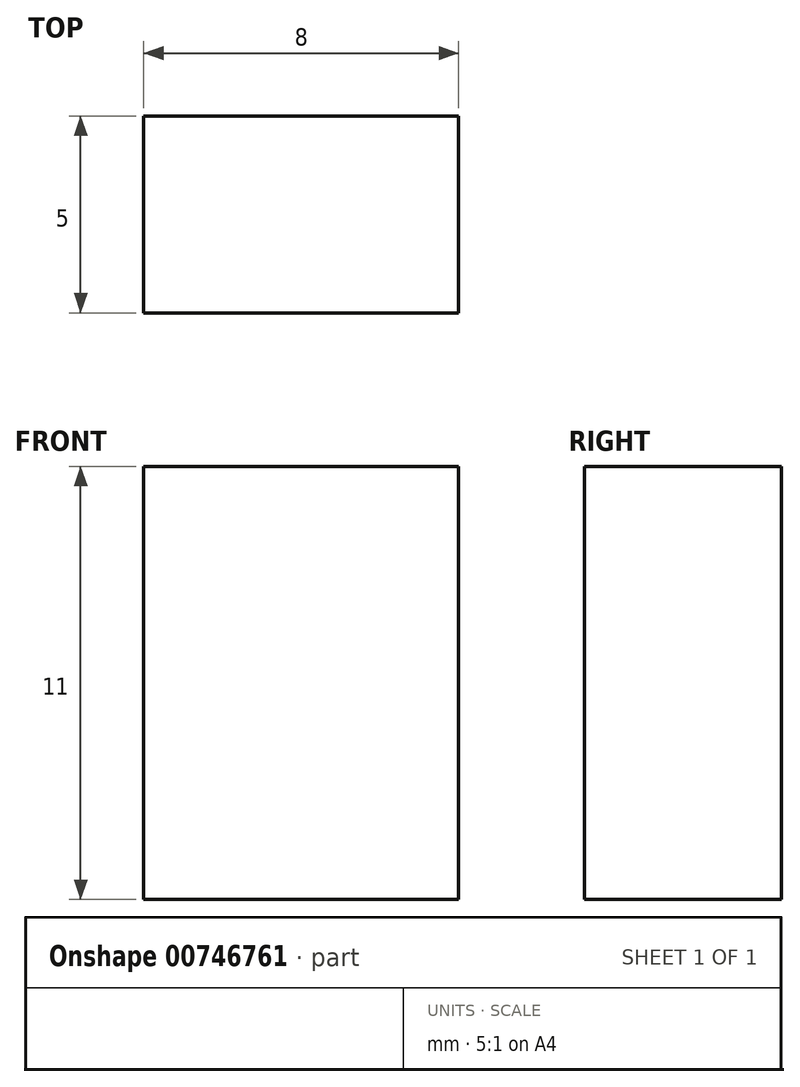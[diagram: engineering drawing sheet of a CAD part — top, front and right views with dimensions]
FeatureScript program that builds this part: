
annotation { "Feature Type Name" : "Feature", "Feature Type Description" : "" }
export const myFeature = defineFeature(function(context is Context, id is Id, definition is map)
    precondition{}
    {
        {
            var Q0;
            Q0=qCreatedBy(makeId("Top.planeOp"),FACE);
            var sketch = newSketch(context, id + "F0", { "sketchPlane" : qUnion([Q0])});
            skLineSegment(sketch, "E0.bottom", {"start": v(-8.77, 4.33) * mm, "end": v(-16.77, 4.33) * mm});
            skLineSegment(sketch, "E0.top", {"start": v(-8.77, 9.33) * mm, "end": v(-16.77, 9.33) * mm});
            skLineSegment(sketch, "E0.left", {"start": v(-8.77, 4.33) * mm, "end": v(-8.77, 9.33) * mm});
            skLineSegment(sketch, "E0.right", {"start": v(-16.77, 4.33) * mm, "end": v(-16.77, 9.33) * mm});
            skSolve(sketch);
        }
        {
            var Q0;
            Q0 = qSketchRegion(id + "F0", true);
            extrude(context, id + "F1", {"entities" : qUnion([Q0]), "depth" : 11 * mm, "offsetDistance" : 25 * mm});
        }
    });
